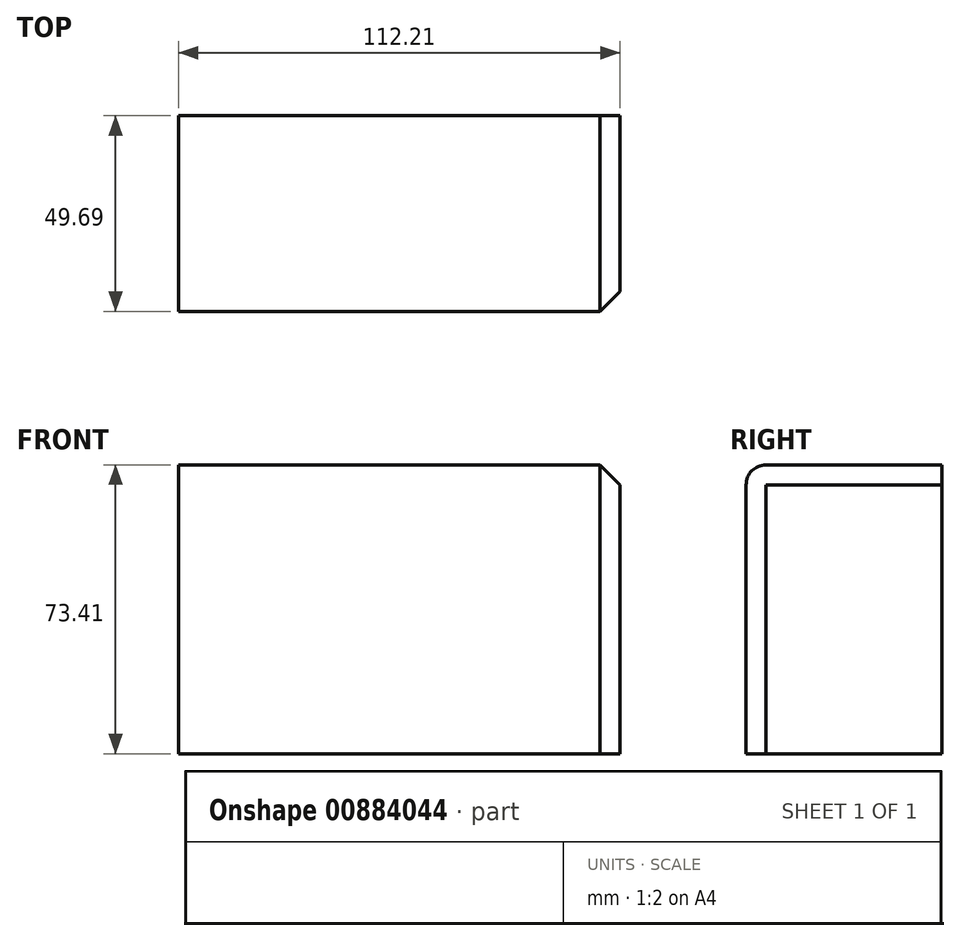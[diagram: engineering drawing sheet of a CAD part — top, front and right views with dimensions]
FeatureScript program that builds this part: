
annotation { "Feature Type Name" : "Feature", "Feature Type Description" : "" }
export const myFeature = defineFeature(function(context is Context, id is Id, definition is map)
    precondition{}
    {
        {
            var Q0;
            Q0=qCreatedBy(makeId("Top.planeOp"),FACE);
            var sketch = newSketch(context, id + "F0", { "sketchPlane" : qUnion([Q0])});
            skLineSegment(sketch, "E0.bottom", {"start": v(-55.7, 0) * mm, "end": v(56.51, 0) * mm});
            skLineSegment(sketch, "E0.top", {"start": v(-55.7, -49.7) * mm, "end": v(56.51, -49.7) * mm});
            skLineSegment(sketch, "E0.left", {"start": v(-55.7, 0) * mm, "end": v(-55.7, -49.7) * mm});
            skLineSegment(sketch, "E0.right", {"start": v(56.51, 0) * mm, "end": v(56.51, -49.7) * mm});
            skSolve(sketch);
        }
        {
            var Q0;
            Q0 = qSketchRegion(id + "F0", true);
            extrude(context, id + "F1", {"entities" : qUnion([Q0]), "depth" : 73.4 * mm, "offsetDistance" : 25.4 * mm});
        }
        {
            var Q0;
            Q0=makeQuery(id+"F1.opExtrude","CAP_EDGE",EDGE,{"disambiguationData":[OSD([sQuery(id+"F0.wireOp",EDGE,"E0.top")])],"isStart":false});
            fillet(context, id + "F2", {"entities" : qUnion([Q0]), "radius" : 5.08 * mm, "tangentPropagation" : true, "allowEdgeOverflow" : false});
        }
        {
            var Q0;
            Q0=makeQuery(id+"F1.opExtrude","CAP_EDGE",EDGE,{"disambiguationData":[OSD([sQuery(id+"F0.wireOp",EDGE,"E0.right")])],"isStart":false});
            chamfer(context, id + "F3", {"entities" : qUnion([Q0]), "width" : 5.08 * mm, "tangentPropagation" : true});
        }
    });
